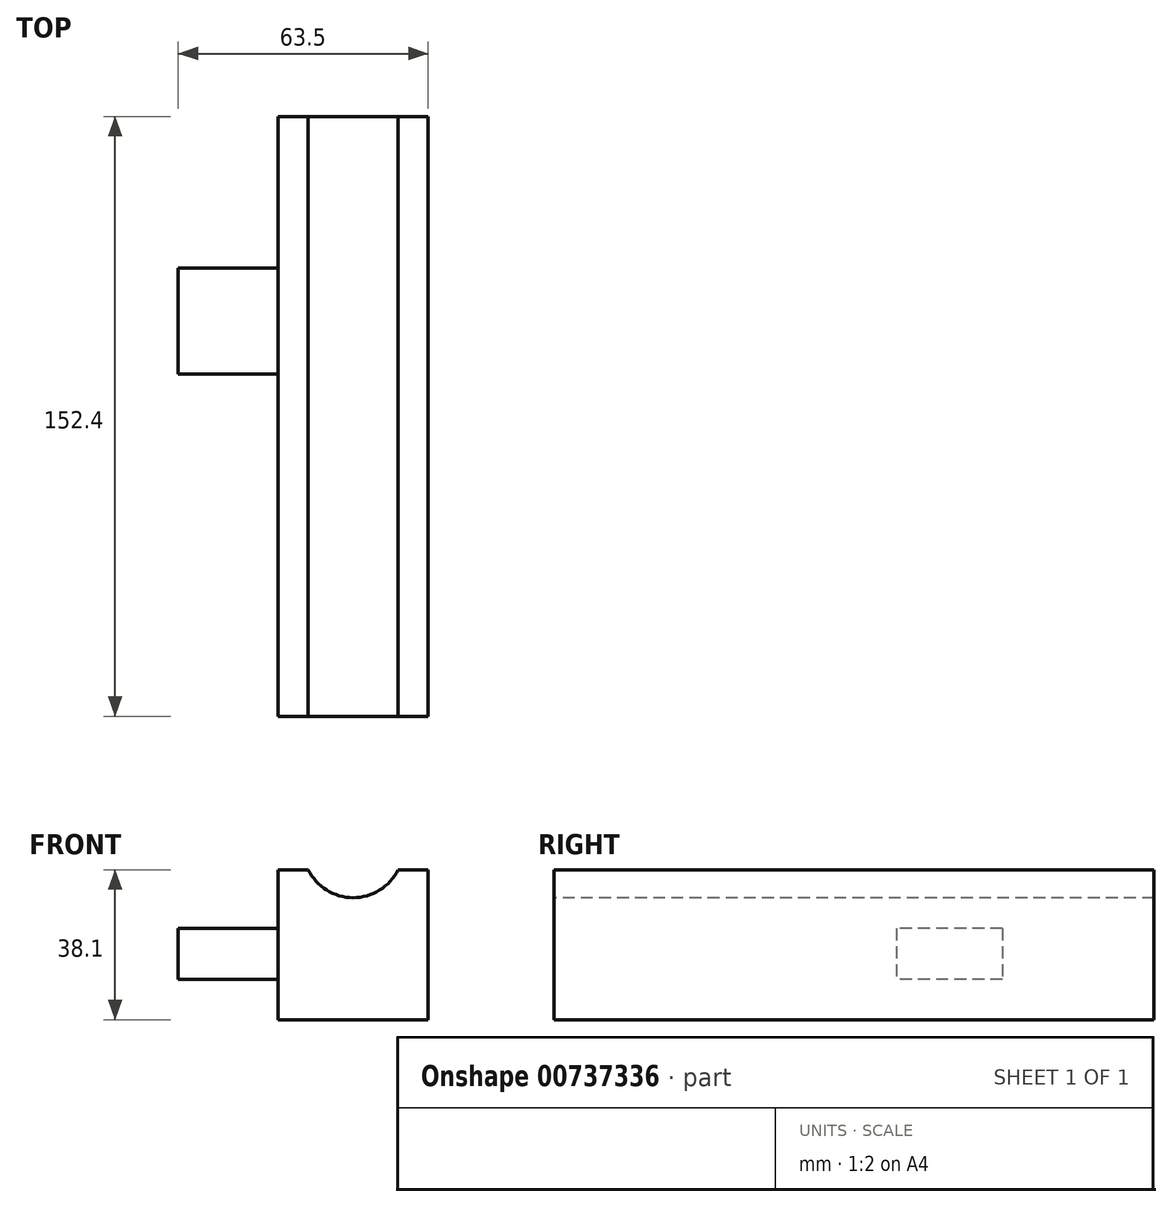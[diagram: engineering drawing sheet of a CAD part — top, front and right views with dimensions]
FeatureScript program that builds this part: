
annotation { "Feature Type Name" : "Feature", "Feature Type Description" : "" }
export const myFeature = defineFeature(function(context is Context, id is Id, definition is map)
    precondition{}
    {
        {
            var Q0;
            Q0=qCreatedBy(makeId("Front.planeOp"),FACE);
            var sketch = newSketch(context, id + "F0", { "sketchPlane" : qUnion([Q0])});
            skLineSegment(sketch, "E0", {"start": v(0, 0) * mm, "end": v(0, -38.1) * mm});
            skLineSegment(sketch, "E1", {"start": v(0, -38.1) * mm, "end": v(38.1, -38.1) * mm});
            skLineSegment(sketch, "E2", {"start": v(38.1, -38.1) * mm, "end": v(38.1, 0) * mm});
            skArc(sketch, "E3", {"start": v(7.62, 0) * mm, "mid": v(19.05, -7.1) * mm, "end": v(30.48, 0) * mm});
            skLineSegment(sketch, "E4", {"start": v(0, 0) * mm, "end": v(7.62, 0) * mm});
            skLineSegment(sketch, "E5", {"start": v(30.48, 0) * mm, "end": v(38.1, 0) * mm});
            skSolve(sketch);
        }
        {
            var Q0;
            Q0 = qSketchRegion(id + "F0", true);
            extrude(context, id + "F1", {"entities" : qUnion([Q0]), "oppositeDirection" : true, "depth" : 152.4 * mm, "offsetDistance" : 25.4 * mm});
        }
        {
            var Q0;
            Q0=makeQuery(id+"F1.opExtrude","SWEPT_FACE",FACE,{"disambiguationData":[OSD([sQuery(id+"F0.wireOp",EDGE,"E0")])]});
            var sketch = newSketch(context, id + "F2", { "sketchPlane" : qUnion([Q0])});
            skLineSegment(sketch, "E6.bottom", {"start": v(-113.89, -14.91) * mm, "end": v(-86.98, -14.91) * mm});
            skLineSegment(sketch, "E6.top", {"start": v(-113.89, -27.91) * mm, "end": v(-86.98, -27.91) * mm});
            skLineSegment(sketch, "E6.left", {"start": v(-113.89, -14.91) * mm, "end": v(-113.89, -27.91) * mm});
            skLineSegment(sketch, "E6.right", {"start": v(-86.98, -14.91) * mm, "end": v(-86.98, -27.91) * mm});
            skSolve(sketch);
        }
        {
            var Q0;
            Q0 = qSketchRegion(id + "F2", true);
            extrude(context, id + "F3", {"entities" : qUnion([Q0]), "operationType" : NewBodyOperationType.ADD, "depth" : 25.4 * mm, "offsetDistance" : 25.4 * mm});
        }
    });
